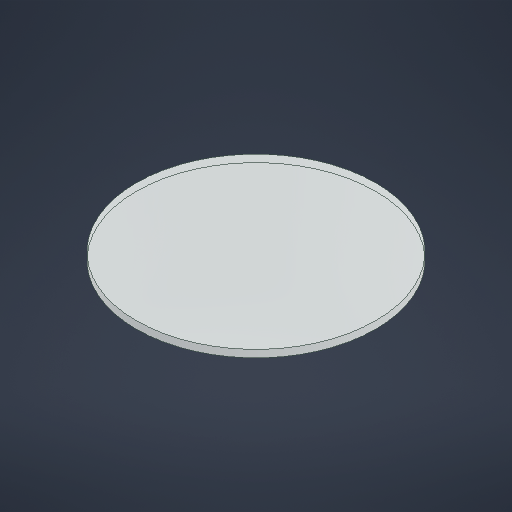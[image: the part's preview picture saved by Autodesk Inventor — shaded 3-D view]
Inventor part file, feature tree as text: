
AUTODESK INVENTOR PART (.ipt)
format: ipt  version: 2025 (Build 290162000, 162)  size: 180,736 bytes
history: native  units: in
note: dims shown in document units (in); Inventor stores cm internally (conversion verified against a paired STEP export)
features: extrude x1, sketch x1
ambient origin geometry x8: Origin, YZ Plane, XZ Plane, XY Plane, X Axis, Y Axis, Z Axis, Center Point
bodies: Solid1 (feature_tree)
feature tree (2):
  extrude  "Extrusion1"  Depth=0.1575in TaperAngle=0.0deg
  sketch  "Sketch1"  dims[d0=5.1181in d1=0.1575in d2=0.0in]
